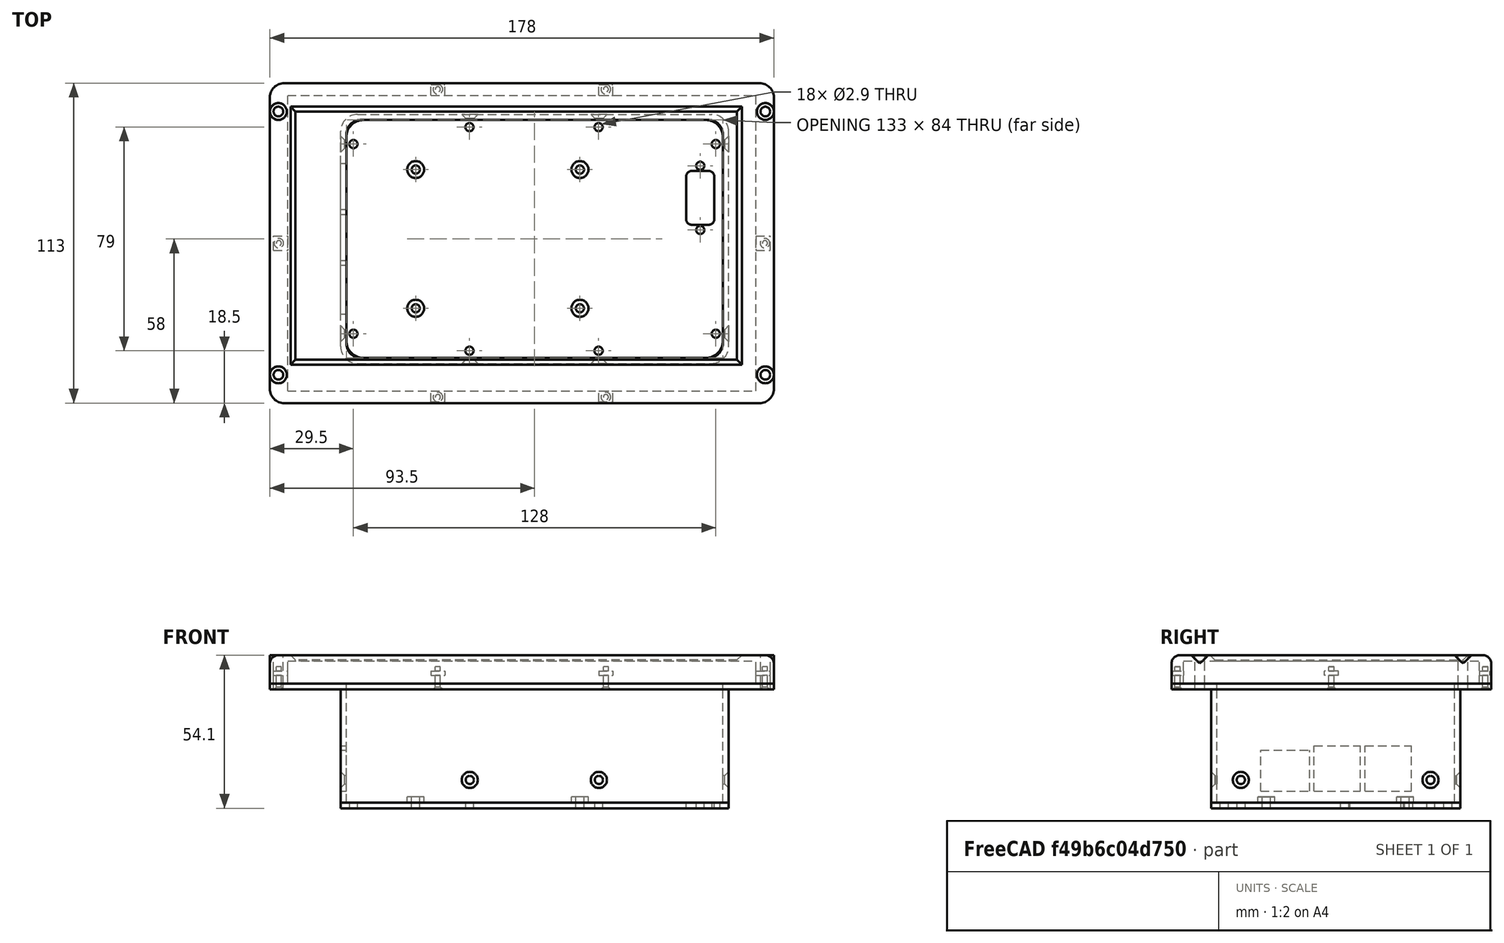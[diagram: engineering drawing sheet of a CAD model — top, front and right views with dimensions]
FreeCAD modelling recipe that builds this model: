
FCSTD DOCUMENT  (FreeCAD 0.20R29410 (Git))
Label: RPI4Soar_V1
License: All rights reserved
LicenseURL: http://en.wikipedia.org/wiki/All_rights_reserved
objects: Part::Cut×53, Part::Cylinder×32, Part::Box×18, Part::Fillet×7, Part::Fuse×5, Part::Chamfer×4, Part::FeaturePython×4, Spreadsheet::Sheet×1
note: 123 computed .brp shape members not serialized (recipe doc carries the construction recipe); baked Part::Feature solids carry a one-line shape summary decoded from their .brp

FEATURE [Spreadsheet::Sheet] Spreadsheet
  cells = A1=Display Abmessungen; C1=Toleranz; A2=Länge / mm; B2=165; C2=0.4; D2==B2 + C2; A3=Breite / mm; B3=104; C3=0.4; D3==B3 + C3; A4=Höhe / mm; B4=7.05; C4=1; D4==B4 + C4; A6=Gehäuse Dimensionen; A7=Länge / mm; B7=178; A8=Breite /mm; B8=113; A9=Höhe / mm; B9=30
FEATURE [Part::Box] Box  label="Würfel"
  AttacherType = Attacher::AttachEngine3D
  Height = 10.05
  Length = 178
  Width = 113
  expr: Height = Spreadsheet.D4 + 2
  expr: Length = Spreadsheet.B7
  expr: Width = Spreadsheet.B8
FEATURE [Part::Box] Box001  label="Würfel001"
  AttacherType = Attacher::AttachEngine3D
  Height = 8.05
  Length = 165.4
  Placement = pos=(6.3,4.3,0) rot=(0,0,1;0rad)
  Width = 104.4
  expr: .Placement.Base.x = (Spreadsheet.B7 - Spreadsheet.D2) / 2
  expr: .Placement.Base.y = (Spreadsheet.B8 - Spreadsheet.D3) / 2
  expr: Height = Spreadsheet.D4
  expr: Length = Spreadsheet.D2
  expr: Width = Spreadsheet.D3
FEATURE [Part::Cylinder] Cylinder  label="Zylinder"
  Angle = 360
  AttacherType = Attacher::AttachEngine3D
  FirstAngle = 0
  Height = 17
  Placement = pos=(3,10,-5) rot=(0,0,1;0rad)
  Radius = 1.7
  SecondAngle = 0
  expr: .Placement.Base.x = (Spreadsheet.B7 - 172) / 2
  expr: .Placement.Base.y = (Spreadsheet.B8 - 93) / 2
FEATURE [Part::Cylinder] Cylinder001  label="Zylinder001"
  Angle = 360
  AttacherType = Attacher::AttachEngine3D
  FirstAngle = 0
  Height = 17
  Placement = pos=(3,103,-5) rot=(0,0,1;0rad)
  Radius = 1.7
  SecondAngle = 0
  expr: .Placement.Base.x = (Spreadsheet.B7 - 172) / 2
  expr: .Placement.Base.y = Spreadsheet.B8 - (Spreadsheet.B8 - 93) / 2
FEATURE [Part::Cylinder] Cylinder002  label="Zylinder002"
  Angle = 360
  AttacherType = Attacher::AttachEngine3D
  FirstAngle = 0
  Height = 17
  Placement = pos=(175,10,-5) rot=(0,0,1;0rad)
  Radius = 1.7
  SecondAngle = 0
  expr: .Placement.Base.x = Spreadsheet.B7 - (Spreadsheet.B7 - 172) / 2
  expr: .Placement.Base.y = (Spreadsheet.B8 - 93) / 2
FEATURE [Part::Cylinder] Cylinder003  label="Zylinder003"
  Angle = 360
  AttacherType = Attacher::AttachEngine3D
  FirstAngle = 0
  Height = 17
  Placement = pos=(175,103,-5) rot=(0,0,1;0rad)
  Radius = 1.7
  SecondAngle = 0
  expr: .Placement.Base.x = Spreadsheet.B7 - (Spreadsheet.B7 - 172) / 2
  expr: .Placement.Base.y = Spreadsheet.B8 - (Spreadsheet.B8 - 93) / 2
FEATURE [Part::Cylinder] Cylinder004  label="Zylinder004"
  Angle = 360
  AttacherType = Attacher::AttachEngine3D
  FirstAngle = 0
  Height = 7.1
  Placement = pos=(3,10,3) rot=(0,0,1;0rad)
  Radius = 2.99
  SecondAngle = 0
  expr: .Placement.Base.x = (Spreadsheet.B7 - 172) / 2
  expr: .Placement.Base.y = (Spreadsheet.B8 - 93) / 2
FEATURE [Part::Cylinder] Cylinder005  label="Zylinder005"
  Angle = 360
  AttacherType = Attacher::AttachEngine3D
  FirstAngle = 0
  Height = 7.1
  Placement = pos=(3,103,3) rot=(0,0,1;0rad)
  Radius = 2.99
  SecondAngle = 0
  expr: .Placement.Base.x = (Spreadsheet.B7 - 172) / 2
  expr: .Placement.Base.y = Spreadsheet.B8 - (Spreadsheet.B8 - 93) / 2
FEATURE [Part::Cylinder] Cylinder006  label="Zylinder006"
  Angle = 360
  AttacherType = Attacher::AttachEngine3D
  FirstAngle = 0
  Height = 7.1
  Placement = pos=(175,10,3) rot=(0,0,1;0rad)
  Radius = 2.99
  SecondAngle = 0
  expr: .Placement.Base.x = Spreadsheet.B7 - (Spreadsheet.B7 - 172) / 2
  expr: .Placement.Base.y = (Spreadsheet.B8 - 93) / 2
FEATURE [Part::Cylinder] Cylinder007  label="Zylinder007"
  Angle = 360
  AttacherType = Attacher::AttachEngine3D
  FirstAngle = 0
  Height = 7.1
  Placement = pos=(175,103,3) rot=(0,0,1;0rad)
  Radius = 2.99
  SecondAngle = 0
  expr: .Placement.Base.x = Spreadsheet.B7 - (Spreadsheet.B7 - 172) / 2
  expr: .Placement.Base.y = Spreadsheet.B8 - (Spreadsheet.B8 - 93) / 2
FEATURE [Part::Box] Box004  label="Würfel004"
  AttacherType = Attacher::AttachEngine3D
  Height = 2
  Length = 178
  Placement = pos=(0,0,-2) rot=(0,0,1;0rad)
  Width = 113
  expr: Length = Spreadsheet.B7
  expr: Width = Spreadsheet.B8
FEATURE [Part::Box] Box005  label="Würfel005"
  AttacherType = Attacher::AttachEngine3D
  Height = 15
  Length = 133
  Placement = pos=(27,16,-14) rot=(0,0,1;0rad)
  Width = 84
FEATURE [Part::Box] Box006  label="Würfel006"
  AttacherType = Attacher::AttachEngine3D
  Height = 7.05
  Length = 156
  Placement = pos=(9,15.3,3) rot=(0,0,1;0rad)
  Width = 87.7
  expr: .Placement.Base.x = 15.5 - 6.5
  expr: .Placement.Base.y = 20.8 - 5.5
  expr: Height = Spreadsheet.B4
FEATURE [Part::Fillet] Fillet003
  Base = -> Box005
  Edges = 4 edges r=5: [Edge1,Edge3,Edge5,Edge7]
FEATURE [Part::Cut] Cut011
  Base = -> Box004
  Tool = -> Fillet003
FEATURE [Part::Cut] Cut012
  Base = -> Cut011
  Tool = -> Cylinder001
FEATURE [Part::Cut] Cut013
  Base = -> Cut012
  Tool = -> Cylinder002
FEATURE [Part::Cut] Cut014
  Base = -> Cut013
  Tool = -> Cylinder003
FEATURE [Part::Cut] Cut015
  Base = -> Cut014
  Tool = -> Cylinder
FEATURE [Part::Fillet] Fillet004
  Base = -> Cut015
  Edges = 4 edges r=5: [Edge1,Edge3,Edge6,Edge23]
FEATURE [Part::Box] Box007  label="Würfel007"
  AttacherType = Attacher::AttachEngine3D
  Height = 40
  Length = 133
  Placement = pos=(27,16,-42) rot=(0,0,1;0rad)
  Width = 84
FEATURE [Part::Box] Box008  label="Würfel008"
  AttacherType = Attacher::AttachEngine3D
  Height = 40
  Length = 137
  Placement = pos=(25,14,-42) rot=(0,0,1;0rad)
  Width = 88
FEATURE [Part::Box] Box010  label="Würfel010"
  AttacherType = Attacher::AttachEngine3D
  Height = 2
  Length = 137
  Placement = pos=(25,14,-44) rot=(0,0,1;0rad)
  Width = 88
FEATURE [Part::Cylinder] Cylinder008  label="Zylinder008"
  Angle = 360
  AttacherType = Attacher::AttachEngine3D
  FirstAngle = 0
  Height = 108
  Placement = pos=(116.2,114,-34) rot=(1,0,0;1.5708rad)
  Radius = 1.45
  SecondAngle = 0
FEATURE [Part::Cylinder] Cylinder010  label="Zylinder010"
  Angle = 360
  AttacherType = Attacher::AttachEngine3D
  FirstAngle = 0
  Height = 155
  Placement = pos=(14,24.5,-34) rot=(0,1,0;1.5708rad)
  Radius = 1.45
  SecondAngle = 0
FEATURE [Part::Cylinder] Cylinder011  label="Zylinder011"
  Angle = 360
  AttacherType = Attacher::AttachEngine3D
  FirstAngle = 0
  Height = 157
  Placement = pos=(14,91.5,-34) rot=(0,1,0;1.5708rad)
  Radius = 1.45
  SecondAngle = 0
FEATURE [Part::Cylinder] Cylinder012  label="Zylinder012"
  Angle = 360
  AttacherType = Attacher::AttachEngine3D
  FirstAngle = 0
  Height = 10
  Placement = pos=(109.5,33.5,-49) rot=(0,0,1;0rad)
  Radius = 1.45
  SecondAngle = 0
  expr: .Placement.Base.y = 35 - 1.5
FEATURE [Part::Cylinder] Cylinder013  label="Zylinder013"
  Angle = 360
  AttacherType = Attacher::AttachEngine3D
  FirstAngle = 0
  Height = 10
  Placement = pos=(51.5,82.5,-49) rot=(0,0,1;0rad)
  Radius = 1.45
  SecondAngle = 0
  expr: .Placement.Base.y = 35 + 49 - 1.5
FEATURE [Part::Cylinder] Cylinder014  label="Zylinder014"
  Angle = 360
  AttacherType = Attacher::AttachEngine3D
  FirstAngle = 0
  Height = 10
  Placement = pos=(51.5,33.5,-49) rot=(0,0,1;0rad)
  Radius = 1.45
  SecondAngle = 0
  expr: .Placement.Base.y = 35 - 1.5
FEATURE [Part::Cylinder] Cylinder015  label="Zylinder015"
  Angle = 360
  AttacherType = Attacher::AttachEngine3D
  FirstAngle = 0
  Height = 10
  Placement = pos=(109.5,82.5,-49) rot=(0,0,1;0rad)
  Radius = 1.45
  SecondAngle = 0
  expr: .Placement.Base.y = 35 + 49 - 1.5
FEATURE [Part::Box] Box017  label="Würfel017"
  AttacherType = Attacher::AttachEngine3D
  Height = 10
  Length = 10
  Placement = pos=(147,63,-49) rot=(0,0,1;0rad)
  Width = 19
FEATURE [Part::Cylinder] Cylinder020  label="Zylinder020"
  Angle = 360
  AttacherType = Attacher::AttachEngine3D
  FirstAngle = 0
  Height = 10
  Placement = pos=(152,83.85,-49) rot=(0,0,1;0rad)
  Radius = 1.45
  SecondAngle = 0
FEATURE [Part::Cylinder] Cylinder021  label="Zylinder021"
  Angle = 360
  AttacherType = Attacher::AttachEngine3D
  FirstAngle = 0
  Height = 10
  Placement = pos=(152,61.15,-49) rot=(0,0,1;0rad)
  Radius = 1.45
  SecondAngle = 0
FEATURE [Part::Cylinder] Cylinder022  label="Zylinder022"
  Angle = 360
  AttacherType = Attacher::AttachEngine3D
  FirstAngle = 0
  Height = 10
  Placement = pos=(59.3333,2.15,-4) rot=(0,0,1;0rad)
  Radius = 0.9
  SecondAngle = 0
  expr: .Placement.Base.x = Spreadsheet.B7 / 3
  expr: .Placement.Base.y = (Spreadsheet.B8 - Spreadsheet.D3) / 4
FEATURE [Part::Cylinder] Cylinder023  label="Zylinder023"
  Angle = 360
  AttacherType = Attacher::AttachEngine3D
  FirstAngle = 0
  Height = 10
  Placement = pos=(118.667,2.15,-4) rot=(0,0,1;0rad)
  Radius = 0.9
  SecondAngle = 0
  expr: .Placement.Base.x = Spreadsheet.B7 / 3 * 2
  expr: .Placement.Base.y = (Spreadsheet.B8 - Spreadsheet.D3) / 4
FEATURE [Part::Box] Box018  label="Würfel018"
  AttacherType = Attacher::AttachEngine3D
  Height = 1.5
  Length = 5
  Placement = pos=(56.8333,0.5,3) rot=(0,0,1;0rad)
  Width = 4
  expr: .Placement.Base.x = Spreadsheet.B7 / 3 - 2.5
FEATURE [Part::Box] Box019  label="Würfel019"
  AttacherType = Attacher::AttachEngine3D
  Height = 1.5
  Length = 5
  Placement = pos=(116.167,0.5,3) rot=(0,0,1;0rad)
  Width = 4
  expr: .Placement.Base.x = Spreadsheet.B7 / 3 * 2 - 2.5
FEATURE [Part::Cylinder] Cylinder024  label="Zylinder024"
  Angle = 360
  AttacherType = Attacher::AttachEngine3D
  FirstAngle = 0
  Height = 10
  Placement = pos=(59.3333,110.85,-4) rot=(0,0,1;0rad)
  Radius = 0.9
  SecondAngle = 0
  expr: .Placement.Base.x = Spreadsheet.B7 / 3
  expr: .Placement.Base.y = Spreadsheet.B8 - (Spreadsheet.B8 - Spreadsheet.D3) / 4
FEATURE [Part::Cylinder] Cylinder025  label="Zylinder025"
  Angle = 360
  AttacherType = Attacher::AttachEngine3D
  FirstAngle = 0
  Height = 10
  Placement = pos=(118.667,110.85,-4) rot=(0,0,1;0rad)
  Radius = 0.9
  SecondAngle = 0
  expr: .Placement.Base.x = Spreadsheet.B7 / 3 * 2
  expr: .Placement.Base.y = Spreadsheet.B8 - (Spreadsheet.B8 - Spreadsheet.D3) / 4
FEATURE [Part::Box] Box020  label="Würfel020"
  AttacherType = Attacher::AttachEngine3D
  Height = 1.5
  Length = 5
  Placement = pos=(56.8333,108.5,3) rot=(0,0,1;0rad)
  Width = 4
  expr: .Placement.Base.x = Spreadsheet.B7 / 3 - 2.5
FEATURE [Part::Cylinder] Cylinder026  label="Zylinder026"
  Angle = 360
  AttacherType = Attacher::AttachEngine3D
  FirstAngle = 0
  Height = 10
  Placement = pos=(3.15,56.5,-4) rot=(0,0,1;0rad)
  Radius = 0.9
  SecondAngle = 0
  expr: .Placement.Base.x = (Spreadsheet.B7 - Spreadsheet.D2) / 4
  expr: .Placement.Base.y = Spreadsheet.B8 / 2
FEATURE [Part::Cylinder] Cylinder027  label="Zylinder027"
  Angle = 360
  AttacherType = Attacher::AttachEngine3D
  FirstAngle = 0
  Height = 10
  Placement = pos=(174.85,56.5,-4) rot=(0,0,1;0rad)
  Radius = 0.9
  SecondAngle = 0
  expr: .Placement.Base.x = Spreadsheet.B7 - (Spreadsheet.B7 - Spreadsheet.D2) / 4
  expr: .Placement.Base.y = Spreadsheet.B8 / 2
FEATURE [Part::Box] Box021  label="Würfel021"
  AttacherType = Attacher::AttachEngine3D
  Height = 1.5
  Length = 6
  Placement = pos=(1.3,54,3) rot=(0,0,1;0rad)
  Width = 5
  expr: .Placement.Base.y = Spreadsheet.B8 / 2 - 2.5
FEATURE [Part::Box] Box022  label="Würfel022"
  AttacherType = Attacher::AttachEngine3D
  Height = 1.5
  Length = 6
  Placement = pos=(170.7,54,3) rot=(0,0,1;0rad)
  Width = 5
  expr: .Placement.Base.y = Spreadsheet.B8 / 2 - 2.5
FEATURE [Part::Cut] Cut
  Base = -> Box
  Tool = -> Box001
FEATURE [Part::Cut] Cut038
  Base = -> Cut
  Tool = -> Box006
FEATURE [Part::Fillet] Fillet
  Base = -> Cut038
  Edges = 4 edges r=5: [Edge1,Edge3,Edge6,Edge15]
FEATURE [Part::Fillet] Fillet012
  Base = -> Fillet
  Edges = 1 edges r=3: [Edge11]
FEATURE [Part::Fuse] Fusion
  Base = -> Fillet012
  Tool = -> Cylinder004
FEATURE [Part::Fuse] Fusion018
  Base = -> Fusion
  Tool = -> Cylinder005
FEATURE [Part::Fuse] Fusion019
  Base = -> Fusion018
  Tool = -> Cylinder006
FEATURE [Part::Fuse] Fusion020
  Base = -> Fusion019
  Tool = -> Cylinder007
FEATURE [Part::Cut] Cut039
  Base = -> Fusion020
  Tool = -> Cylinder
FEATURE [Part::Cut] Cut040
  Base = -> Cut039
  Tool = -> Cylinder001
FEATURE [Part::Cut] Cut041
  Base = -> Cut040
  Tool = -> Cylinder002
FEATURE [Part::Cut] Cut042
  Base = -> Cut041
  Tool = -> Cylinder003
FEATURE [Part::Chamfer] Chamfer
  Base = -> Cut042
  Edges = 2 edges r=1.7: [Edge28,Edge31]
FEATURE [Part::Chamfer] Chamfer004
  Base = -> Chamfer
  Edges = 6 edges r=1.7: [Edge1,Edge2,Edge4,Edge5,Edge7,Edge8]
FEATURE [Part::Cut] Cut043
  Base = -> Chamfer004
  Tool = -> Cylinder022
FEATURE [Part::Cut] Cut044
  Base = -> Cut043
  Tool = -> Cylinder023
FEATURE [Part::Cut] Cut045
  Base = -> Cut044
  Tool = -> Cylinder024
FEATURE [Part::Cut] Cut046
  Base = -> Cut045
  Tool = -> Cylinder025
FEATURE [Part::Cut] Cut047
  Base = -> Cut046
  Tool = -> Cylinder026
FEATURE [Part::Cut] Cut048
  Base = -> Cut047
  Tool = -> Cylinder027
FEATURE [Part::Cut] Cut049
  Base = -> Cut048
  Tool = -> Box018
FEATURE [Part::Cut] Cut050
  Base = -> Cut049
  Tool = -> Box019
FEATURE [Part::Cut] Cut051
  Base = -> Cut050
  Tool = -> Box020
FEATURE [Part::Cut] Cut052
  Base = -> Cut051
  Tool = -> Box021
FEATURE [Part::Cut] Cut053
  Base = -> Cut052
  Tool = -> Box022
FEATURE [Part::Cut] Cut054
  Base = -> Box008
  Tool = -> Box007
FEATURE [Part::Cut] Cut060
  Base = -> Fillet004
  Tool = -> Cylinder022
FEATURE [Part::Cut] Cut061
  Base = -> Cut060
  Tool = -> Cylinder022
FEATURE [Part::Cut] Cut062
  Base = -> Cut061
  Tool = -> Cylinder024
FEATURE [Part::Cut] Cut063
  Base = -> Cut062
  Tool = -> Cylinder025
FEATURE [Part::Cut] Cut064
  Base = -> Cut063
  Tool = -> Cylinder026
FEATURE [Part::Cut] Cut065
  Base = -> Cut064
  Tool = -> Cylinder027
FEATURE [Part::Cut] Cut066
  Base = -> Cut065
  Tool = -> Cylinder023
FEATURE [Part::Box] Box023  label="Würfel023"
  AttacherType = Attacher::AttachEngine3D
  Height = 1.5
  Length = 5
  Placement = pos=(116.167,108.5,3) rot=(0,0,1;0rad)
  Width = 4
  expr: .Placement.Base.x = Spreadsheet.B7 / 3 * 2 - 2.5
FEATURE [Part::Cut] Cut083  label="Frame"
  Base = -> Cut053
  Tool = -> Box023
FEATURE [Part::Cylinder] Cylinder032  label="Zylinder032"
  Angle = 360
  AttacherType = Attacher::AttachEngine3D
  FirstAngle = 0
  Height = 108
  Placement = pos=(70.6,114,-34) rot=(1,0,0;1.5708rad)
  Radius = 1.45
  SecondAngle = 0
FEATURE [Part::Cylinder] Cylinder033  label="Zylinder033"
  Angle = 360
  AttacherType = Attacher::AttachEngine3D
  FirstAngle = 0
  Height = 10
  Placement = pos=(116.1,97.5,-49) rot=(0,0,1;0rad)
  Radius = 1.45
  SecondAngle = 0
FEATURE [Part::Cylinder] Cylinder034  label="Zylinder034"
  Angle = 360
  AttacherType = Attacher::AttachEngine3D
  FirstAngle = 0
  Height = 10
  Placement = pos=(116.1,18.5,-49) rot=(0,0,1;0rad)
  Radius = 1.45
  SecondAngle = 0
FEATURE [Part::Cylinder] Cylinder035  label="Zylinder035"
  Angle = 360
  AttacherType = Attacher::AttachEngine3D
  FirstAngle = 0
  Height = 10
  Placement = pos=(70.5,97.5,-49) rot=(0,0,1;0rad)
  Radius = 1.45
  SecondAngle = 0
FEATURE [Part::Cylinder] Cylinder036  label="Zylinder036"
  Angle = 360
  AttacherType = Attacher::AttachEngine3D
  FirstAngle = 0
  Height = 10
  Placement = pos=(70.5,18.5,-49) rot=(0,0,1;0rad)
  Radius = 1.45
  SecondAngle = 0
FEATURE [Part::Cylinder] Cylinder037  label="Zylinder037"
  Angle = 360
  AttacherType = Attacher::AttachEngine3D
  FirstAngle = 0
  Height = 10
  Placement = pos=(29.5,91.5,-49) rot=(0,0,1;0rad)
  Radius = 1.45
  SecondAngle = 0
FEATURE [Part::Cylinder] Cylinder038  label="Zylinder038"
  Angle = 360
  AttacherType = Attacher::AttachEngine3D
  FirstAngle = 0
  Height = 10
  Placement = pos=(157.5,91.5,-49) rot=(0,0,1;0rad)
  Radius = 1.45
  SecondAngle = 0
FEATURE [Part::Cylinder] Cylinder039  label="Zylinder039"
  Angle = 360
  AttacherType = Attacher::AttachEngine3D
  FirstAngle = 0
  Height = 10
  Placement = pos=(157.5,24.5,-49) rot=(0,0,1;0rad)
  Radius = 1.45
  SecondAngle = 0
FEATURE [Part::Cylinder] Cylinder040  label="Zylinder040"
  Angle = 360
  AttacherType = Attacher::AttachEngine3D
  FirstAngle = 0
  Height = 10
  Placement = pos=(29.5,24.5,-49) rot=(0,0,1;0rad)
  Radius = 1.45
  SecondAngle = 0
FEATURE [Part::Cut] Cut089
  Base = -> Cut054
  Tool = -> Cylinder008
FEATURE [Part::Cut] Cut090
  Base = -> Cut089
  Tool = -> Cylinder010
FEATURE [Part::Cut] Cut091
  Base = -> Cut090
  Tool = -> Cylinder011
FEATURE [Part::Cut] Cut092
  Base = -> Cut091
  Tool = -> Cylinder032
FEATURE [Part::Fillet] Fillet013
  Base = -> Cut092
  Edges = 8 edges r=6: [Edge1,Edge4,Edge8,Edge24,Edge37,Edge38,Edge39,Edge40]
FEATURE [Part::Fillet] Fillet014
  Base = -> Box010
  Edges = 4 edges r=6: [Edge1,Edge3,Edge5,Edge7]
FEATURE [Part::Cut] Cut093
  Base = -> Fillet014
  Tool = -> Cylinder033
FEATURE [Part::Cut] Cut094
  Base = -> Cut093
  Tool = -> Cylinder034
FEATURE [Part::Cut] Cut095
  Base = -> Cut094
  Tool = -> Cylinder035
FEATURE [Part::Cut] Cut096
  Base = -> Cut095
  Tool = -> Cylinder036
FEATURE [Part::Cut] Cut097
  Base = -> Cut096
  Tool = -> Cylinder037
FEATURE [Part::Cut] Cut098
  Base = -> Cut097
  Tool = -> Cylinder038
FEATURE [Part::Cut] Cut099
  Base = -> Cut098
  Tool = -> Cylinder039
FEATURE [Part::Cut] Cut100
  Base = -> Cut099
  Tool = -> Cylinder040
FEATURE [Part::Cut] Cut101
  Base = -> Cut100
  Tool = -> Cylinder012
FEATURE [Part::Cut] Cut102
  Base = -> Cut101
  Tool = -> Cylinder013
FEATURE [Part::Cut] Cut103
  Base = -> Cut102
  Tool = -> Cylinder014
FEATURE [Part::Cut] Cut104
  Base = -> Cut103
  Tool = -> Cylinder015
FEATURE [Part::FeaturePython] Tube  label="Spacer"  # WARN: FeaturePython — macro-defined, semantics opaque (R4)
  AttacherType = Attacher::AttachEngine3D
  Height = 2
  InnerRadius = 1.45
  OuterRadius = 3
  Placement = pos=(109.5,33.5,-42) rot=(0,0,1;0rad)
FEATURE [Part::Chamfer] Chamfer005
  Base = -> Fillet013
  Edges = 8 edges r=1.4: [Edge5,Edge6,Edge44,Edge45,Edge47,Edge48,Edge51,Edge52]
FEATURE [Part::Fuse] Fusion021
  Base = -> Chamfer005
  Tool = -> Cut066
FEATURE [Part::Chamfer] Chamfer006
  Base = -> Fusion021
  Edges = 6 edges r=0.8: [Edge18,Edge19,Edge21,Edge23,Edge31,Edge32]
FEATURE [Part::Box] Box034  label="Würfel034"
  AttacherType = Attacher::AttachEngine3D
  Height = 14.5
  Length = 2
  Placement = pos=(25,31.5,-38) rot=(0,0,1;0rad)
  Width = 17.3
FEATURE [Part::Box] Box035  label="Würfel035"
  AttacherType = Attacher::AttachEngine3D
  Height = 16
  Length = 2
  Placement = pos=(25,50.4,-38) rot=(0,0,1;0rad)
  Width = 16.3
FEATURE [Part::Box] Box036  label="Würfel036"
  AttacherType = Attacher::AttachEngine3D
  Height = 16
  Length = 2
  Placement = pos=(25,68.4,-38) rot=(0,0,1;0rad)
  Width = 16.3
FEATURE [Part::Cut] Cut105
  Base = -> Chamfer006
  Tool = -> Box034
FEATURE [Part::Cut] Cut106
  Base = -> Cut105
  Tool = -> Box035
FEATURE [Part::Cut] Cut107  label="Housing"
  Base = -> Cut106
  Tool = -> Box036
FEATURE [Part::Fillet] Fillet015
  Base = -> Box017
  Edges = 4 edges r=2: [Edge1,Edge3,Edge5,Edge7]
FEATURE [Part::Cut] Cut108
  Base = -> Cut104
  Tool = -> Fillet015
FEATURE [Part::Cut] Cut109
  Base = -> Cut108
  Tool = -> Cylinder020
FEATURE [Part::Cut] Cut110  label="Backplate"
  Base = -> Cut109
  Tool = -> Cylinder021
FEATURE [Part::FeaturePython] Tube001  label="Spacer1"  # WARN: FeaturePython — macro-defined, semantics opaque (R4)
  AttacherType = Attacher::AttachEngine3D
  Height = 2
  InnerRadius = 1.45
  OuterRadius = 3
  Placement = pos=(51.5,33.5,-42) rot=(0,0,1;0rad)
FEATURE [Part::FeaturePython] Tube002  label="Spacer2"  # WARN: FeaturePython — macro-defined, semantics opaque (R4)
  AttacherType = Attacher::AttachEngine3D
  Height = 2
  InnerRadius = 1.45
  OuterRadius = 3
  Placement = pos=(109.5,82.5,-42) rot=(0,0,1;0rad)
FEATURE [Part::FeaturePython] Tube003  label="Spacer3"  # WARN: FeaturePython — macro-defined, semantics opaque (R4)
  AttacherType = Attacher::AttachEngine3D
  Height = 2
  InnerRadius = 1.45
  OuterRadius = 3
  Placement = pos=(51.5,82.5,-42) rot=(0,0,1;0rad)
